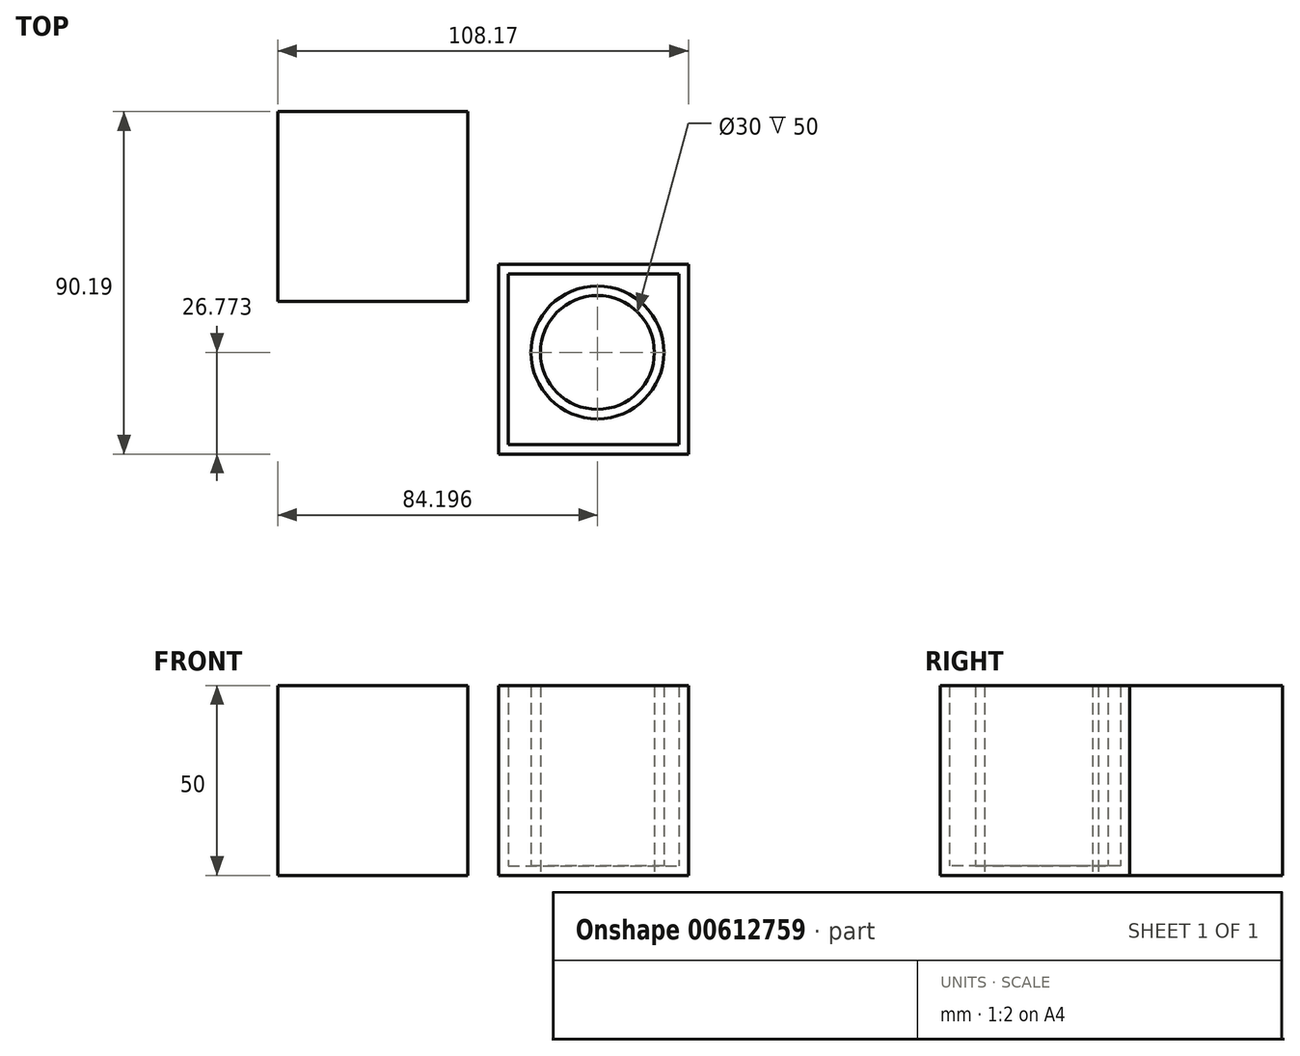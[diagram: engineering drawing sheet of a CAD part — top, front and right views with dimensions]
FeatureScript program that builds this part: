
annotation { "Feature Type Name" : "Feature", "Feature Type Description" : "" }
export const myFeature = defineFeature(function(context is Context, id is Id, definition is map)
    precondition{}
    {
        {
            var Q0;
            Q0=qCreatedBy(makeId("Top.planeOp"),FACE);
            var sketch = newSketch(context, id + "F0", { "sketchPlane" : qUnion([Q0])});
            skLineSegment(sketch, "E0.bottom", {"start": v(0, 0) * mm, "end": v(-50, 0) * mm});
            skLineSegment(sketch, "E0.top", {"start": v(0, 50) * mm, "end": v(-50, 50) * mm});
            skLineSegment(sketch, "E0.left", {"start": v(0, 0) * mm, "end": v(0, 50) * mm});
            skLineSegment(sketch, "E0.right", {"start": v(-50, 0) * mm, "end": v(-50, 50) * mm});
            skSolve(sketch);
        }
        {
            var Q0;
            Q0=makeQuery(id+"F0.imprint","IMPRINT",FACE,{"disambiguationData":[TD([[makeQuery(id+"F0.imprint","IMPRINT",EDGE,{"derivedFrom":sQuery(id+"F0.wireOp",EDGE,"E0.bottom")}),-1.0]])]});
            extrude(context, id + "F1", {"entities" : qUnion([Q0]), "depth" : 50 * mm, "offsetDistance" : 25 * mm});
        }
        {
            var Q0;
            Q0=qCreatedBy(makeId("Top.planeOp"),FACE);
            var sketch = newSketch(context, id + "F2", { "sketchPlane" : qUnion([Q0])});
            skLineSegment(sketch, "E1.bottom", {"start": v(8.17, 9.8) * mm, "end": v(58.17, 9.8) * mm});
            skLineSegment(sketch, "E1.top", {"start": v(8.17, -40.2) * mm, "end": v(58.17, -40.2) * mm});
            skLineSegment(sketch, "E1.left", {"start": v(8.17, 9.8) * mm, "end": v(8.17, -40.2) * mm});
            skLineSegment(sketch, "E1.right", {"start": v(58.17, 9.8) * mm, "end": v(58.17, -40.2) * mm});
            skCircle(sketch, "E2", {"center": v(34.2, -13.42) * mm, "radius": 15 * mm});
            skSolve(sketch);
        }
        {
            var Q0;
            Q0 = qSketchRegion(id + "F2", true);
            extrude(context, id + "F3", {"entities" : qUnion([Q0]), "depth" : 50 * mm, "offsetDistance" : 25 * mm});
        }
        {
            var Q0;
            Q0=makeQuery(id+"F3.opExtrude","CAP_FACE",FACE,{"disambiguationData":[OSD([sQuery(id+"F2.wireOp",EDGE,"E1.bottom"),sQuery(id+"F2.wireOp",EDGE,"E1.top"),sQuery(id+"F2.wireOp",EDGE,"E1.left"),sQuery(id+"F2.wireOp",EDGE,"E1.right"),sQuery(id+"F2.wireOp",EDGE,"E2")])],"isStart":false});
            shell(context, id + "F4", {"entities" : qUnion([Q0]), "thickness" : 2.5 * mm});
        }
    });
